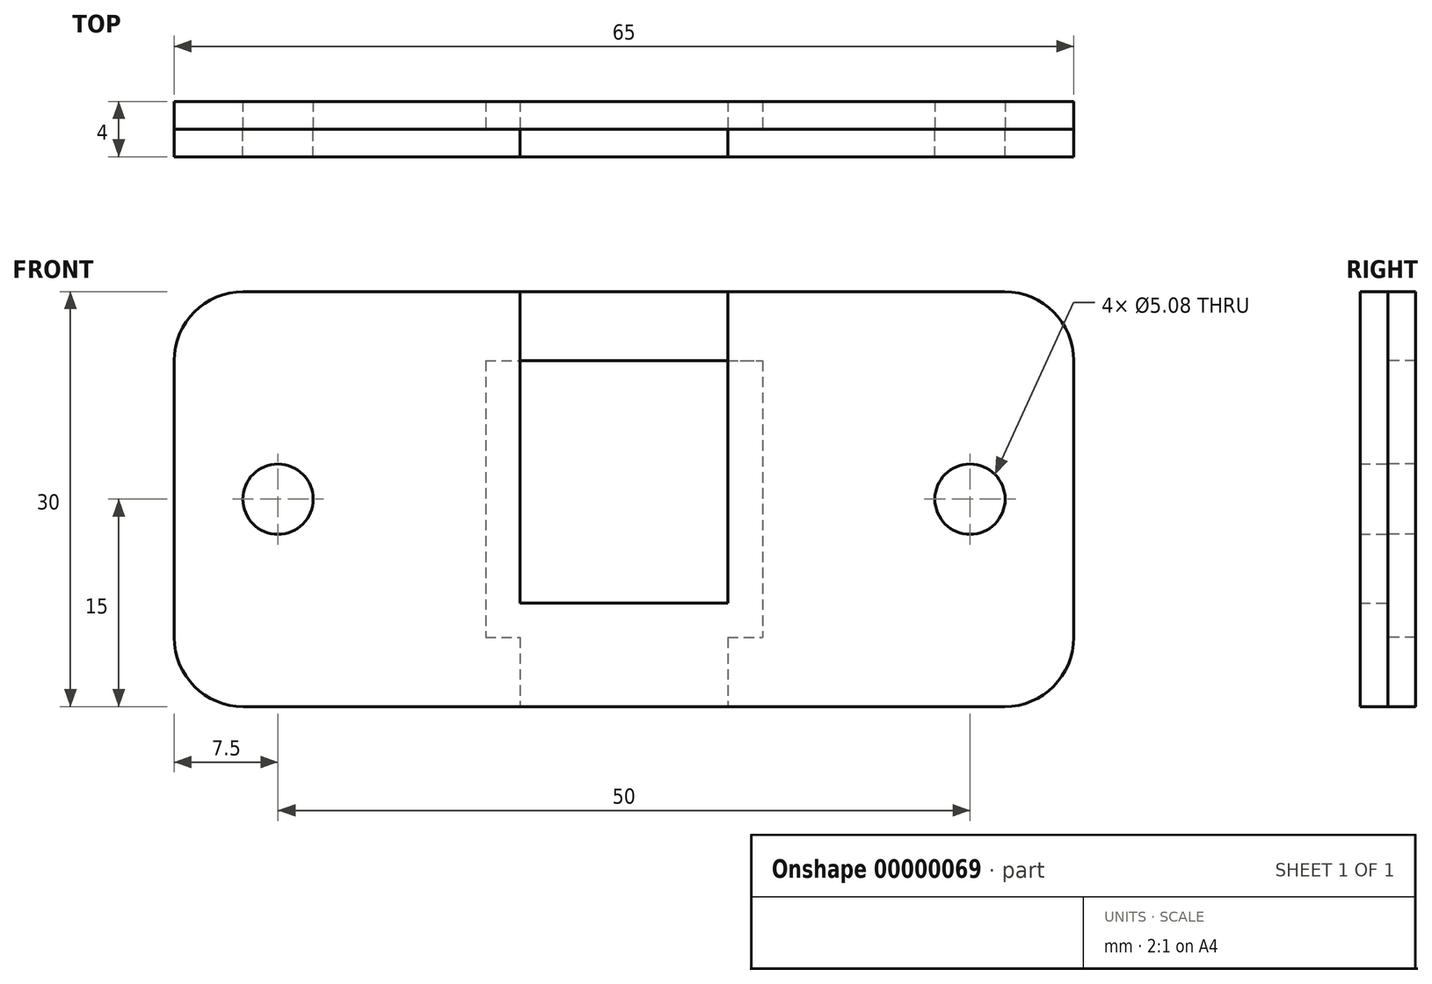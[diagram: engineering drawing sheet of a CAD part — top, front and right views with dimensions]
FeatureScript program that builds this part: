
annotation { "Feature Type Name" : "Feature", "Feature Type Description" : "" }
export const myFeature = defineFeature(function(context is Context, id is Id, definition is map)
    precondition{}
    {
        {
            var Q0;
            Q0=qCreatedBy(makeId("Front.planeOp"),FACE);
            var sketch = newSketch(context, id + "F0", { "sketchPlane" : qUnion([Q0])});
            skLineSegment(sketch, "E0.rect.bottom", {"start": v(-7.5, 7.5) * mm, "end": v(7.5, 7.5) * mm});
            skLineSegment(sketch, "E0.rect.top", {"start": v(-7.5, -7.5) * mm, "end": v(7.5, -7.5) * mm});
            skLineSegment(sketch, "E0.rect.left", {"start": v(-7.5, 7.5) * mm, "end": v(-7.5, -7.5) * mm});
            skLineSegment(sketch, "E0.rect.right", {"start": v(7.5, 7.5) * mm, "end": v(7.5, -7.5) * mm});
            skPoint(sketch, "E0.rect.middle", {"position": v(0, 0) * mm});
            skLineSegment(sketch, "E1.rect.bottom", {"start": v(-10, 10) * mm, "end": v(10, 10) * mm});
            skLineSegment(sketch, "E1.rect.top", {"start": v(-10, -10) * mm, "end": v(10, -10) * mm});
            skLineSegment(sketch, "E1.rect.left", {"start": v(-10, 10) * mm, "end": v(-10, -10) * mm});
            skLineSegment(sketch, "E1.rect.right", {"start": v(10, 10) * mm, "end": v(10, -10) * mm});
            skLineSegment(sketch, "E2.rect.bottom", {"start": v(-27.5, 15) * mm, "end": v(27.5, 15) * mm});
            skLineSegment(sketch, "E2.rect.top", {"start": v(-27.5, -15) * mm, "end": v(27.5, -15) * mm});
            skLineSegment(sketch, "E2.rect.left", {"start": v(-32.5, 10) * mm, "end": v(-32.5, -10) * mm});
            skLineSegment(sketch, "E2.rect.right", {"start": v(32.5, 10) * mm, "end": v(32.5, -10) * mm});
            skLineSegment(sketch, "E3", {"start": v(-7.5, 7.5) * mm, "end": v(-7.5, 15) * mm});
            skLineSegment(sketch, "E4", {"start": v(7.5, 7.5) * mm, "end": v(7.5, 15) * mm});
            skLineSegment(sketch, "E5", {"start": v(-7.5, -7.5) * mm, "end": v(-7.5, -15) * mm});
            skLineSegment(sketch, "E6", {"start": v(7.5, -7.5) * mm, "end": v(7.5, -15) * mm});
            skCircle(sketch, "E7", {"center": v(-25, 0) * mm, "radius": 2.54 * mm});
            skLineSegment(sketch, "E8", {"start": v(0, 0) * mm, "end": v(0, 15) * mm, "construction": true});
            skCircle(sketch, "E9.0.MirrorC", {"center": v(25, 0) * mm, "radius": 2.54 * mm});
            skPoint(sketch, "E10.visualSharp", {"position": v(-32.5, 15) * mm});
            skArc(sketch, "E10.filletArc", {"start": v(-27.5, 15) * mm, "mid": v(-31.04, 13.54) * mm, "end": v(-32.5, 10) * mm});
            skPoint(sketch, "E11.visualSharp", {"position": v(-32.5, -15) * mm});
            skArc(sketch, "E11.filletArc", {"start": v(-32.5, -10) * mm, "mid": v(-31.04, -13.54) * mm, "end": v(-27.5, -15) * mm});
            skPoint(sketch, "E12.visualSharp", {"position": v(32.5, -15) * mm});
            skArc(sketch, "E12.filletArc", {"start": v(27.5, -15) * mm, "mid": v(31.04, -13.54) * mm, "end": v(32.5, -10) * mm});
            skPoint(sketch, "E13.visualSharp", {"position": v(32.5, 15) * mm});
            skArc(sketch, "E13.filletArc", {"start": v(32.5, 10) * mm, "mid": v(31.04, 13.54) * mm, "end": v(27.5, 15) * mm});
            skSolve(sketch);
        }
        {
            var Q0;
            {var subQ11=sQuery(id+"F0.wireOp",EDGE,"E1.rect.left");Q0=makeQuery(id+"F0.imprint","IMPRINT",FACE,{"disambiguationData":[TD([[makeQuery(id+"F0.imprint","IMPRINT",EDGE,{"derivedFrom":subQ11}),-1.0]])]});}
            var Q1;
            {var subQ1=sQuery(id+"F0.wireOp",EDGE,"E1.rect.top");var subQ5=sQuery(id+"F0.wireOp",EDGE,"E5");var subQ6=makeQuery(id+"F0.imprint","INTERSECT",VERTEX,{"derivedFrom":[subQ1,subQ5]});Q1=makeQuery(id+"F0.imprint","IMPRINT",FACE,{"disambiguationData":[TD([[makeQuery(id+"F0.imprint","IMPRINT",EDGE,{"disambiguationData":[TD([[subQ6,-1.0]])],"derivedFrom":subQ1}),-1.0]])]});}
            var Q2;
            {var subQ11=sQuery(id+"F0.wireOp",EDGE,"E1.rect.right");Q2=makeQuery(id+"F0.imprint","IMPRINT",FACE,{"disambiguationData":[TD([[makeQuery(id+"F0.imprint","IMPRINT",EDGE,{"derivedFrom":subQ11}),1.0]])]});}
            var Q3;
            {var subQ3=sQuery(id+"F0.wireOp",EDGE,"E0.rect.right");Q3=makeQuery(id+"F0.imprint","IMPRINT",FACE,{"disambiguationData":[TD([[makeQuery(id+"F0.imprint","IMPRINT",EDGE,{"derivedFrom":subQ3}),1.0]])]});}
            var Q4;
            {var subQ3=sQuery(id+"F0.wireOp",EDGE,"E0.rect.left");Q4=makeQuery(id+"F0.imprint","IMPRINT",FACE,{"disambiguationData":[TD([[makeQuery(id+"F0.imprint","IMPRINT",EDGE,{"derivedFrom":subQ3}),-1.0]])]});}
            var Q5;
            {var subQ3=sQuery(id+"F0.wireOp",EDGE,"E0.rect.top");Q5=makeQuery(id+"F0.imprint","IMPRINT",FACE,{"disambiguationData":[TD([[makeQuery(id+"F0.imprint","IMPRINT",EDGE,{"derivedFrom":subQ3}),-1.0]])]});}
            extrude(context, id + "F1", {"entities" : qUnion([Q0, Q1, Q2, Q3, Q4, Q5]), "depth" : 2 * mm});
        }
        {
            var Q0;
            {var subQ11=sQuery(id+"F0.wireOp",EDGE,"E1.rect.left");Q0=makeQuery(id+"F0.imprint","IMPRINT",FACE,{"disambiguationData":[TD([[makeQuery(id+"F0.imprint","IMPRINT",EDGE,{"derivedFrom":subQ11}),-1.0]])]});}
            var Q1;
            {var subQ1=sQuery(id+"F0.wireOp",EDGE,"E1.rect.bottom");var subQ5=sQuery(id+"F0.wireOp",EDGE,"E3");var subQ6=makeQuery(id+"F0.imprint","INTERSECT",VERTEX,{"derivedFrom":[subQ1,subQ5]});Q1=makeQuery(id+"F0.imprint","IMPRINT",FACE,{"disambiguationData":[TD([[makeQuery(id+"F0.imprint","IMPRINT",EDGE,{"disambiguationData":[TD([[subQ6,-1.0]])],"derivedFrom":subQ1}),1.0]])]});}
            var Q2;
            {var subQ11=sQuery(id+"F0.wireOp",EDGE,"E1.rect.right");Q2=makeQuery(id+"F0.imprint","IMPRINT",FACE,{"disambiguationData":[TD([[makeQuery(id+"F0.imprint","IMPRINT",EDGE,{"derivedFrom":subQ11}),1.0]])]});}
            extrude(context, id + "F2", {"entities" : qUnion([Q0, Q1, Q2]), "oppositeDirection" : true, "depth" : 2 * mm});
        }
    });
